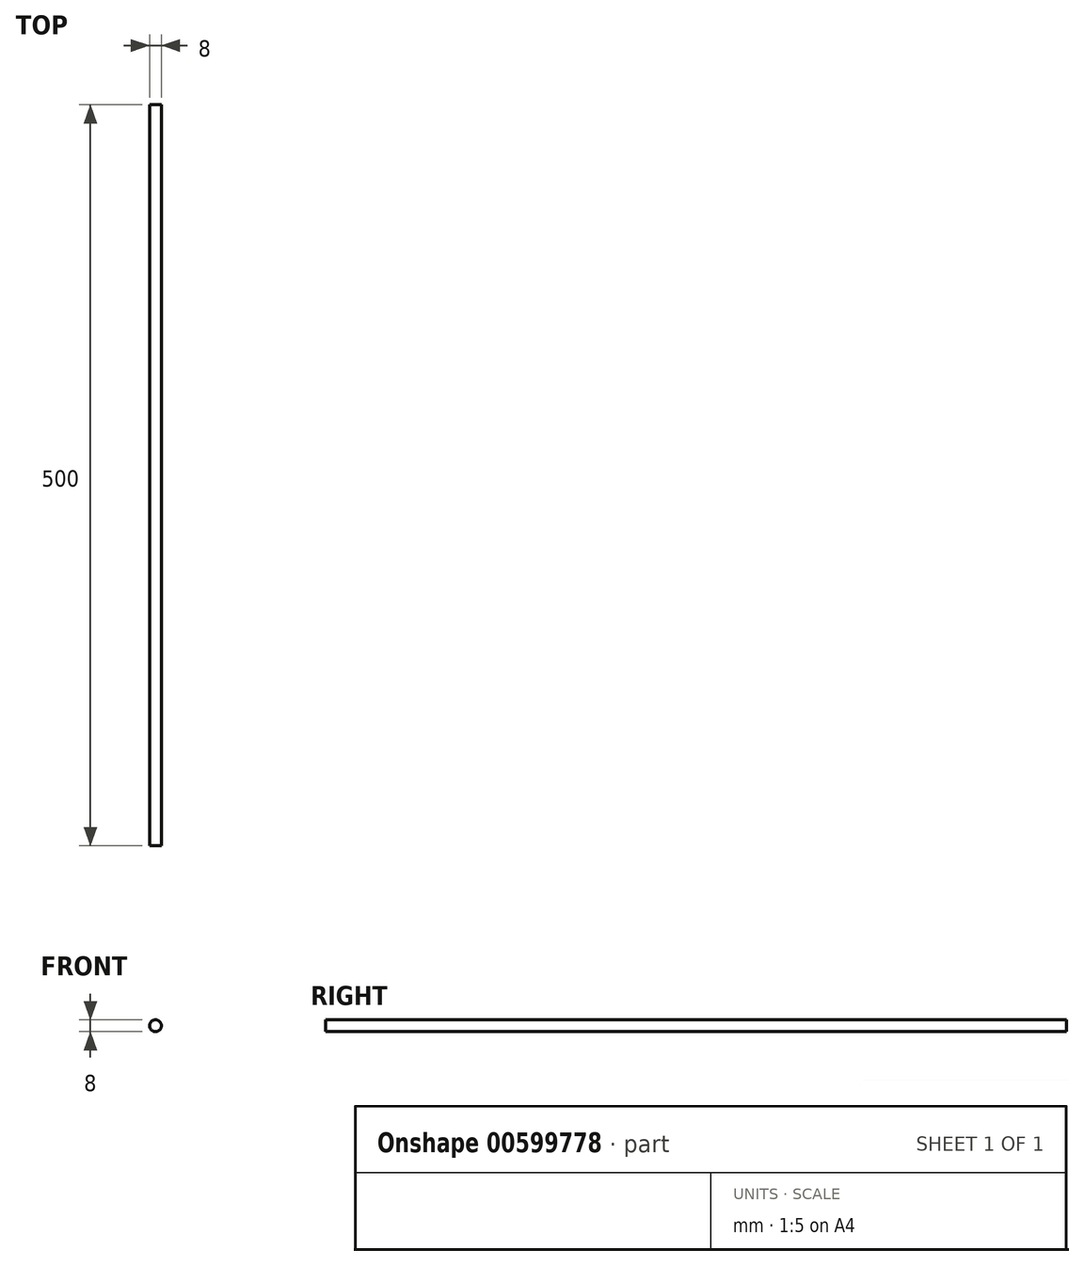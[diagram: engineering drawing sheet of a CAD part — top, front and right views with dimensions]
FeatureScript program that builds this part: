
annotation { "Feature Type Name" : "Feature", "Feature Type Description" : "" }
export const myFeature = defineFeature(function(context is Context, id is Id, definition is map)
    precondition{}
    {
        {
            var Q0;
            Q0=qCreatedBy(makeId("Front.planeOp"),FACE);
            var sketch = newSketch(context, id + "F0", { "sketchPlane" : qUnion([Q0])});
            skCircle(sketch, "E0", {"center": v(0, 0) * mm, "radius": 4 * mm});
            skSolve(sketch);
        }
        {
            var Q0;
            Q0 = qSketchRegion(id + "F0", true);
            extrude(context, id + "F1", {"entities" : qUnion([Q0]), "oppositeDirection" : true, "depth" : 500 * mm, "offsetDistance" : 25.4 * mm});
        }
    });
